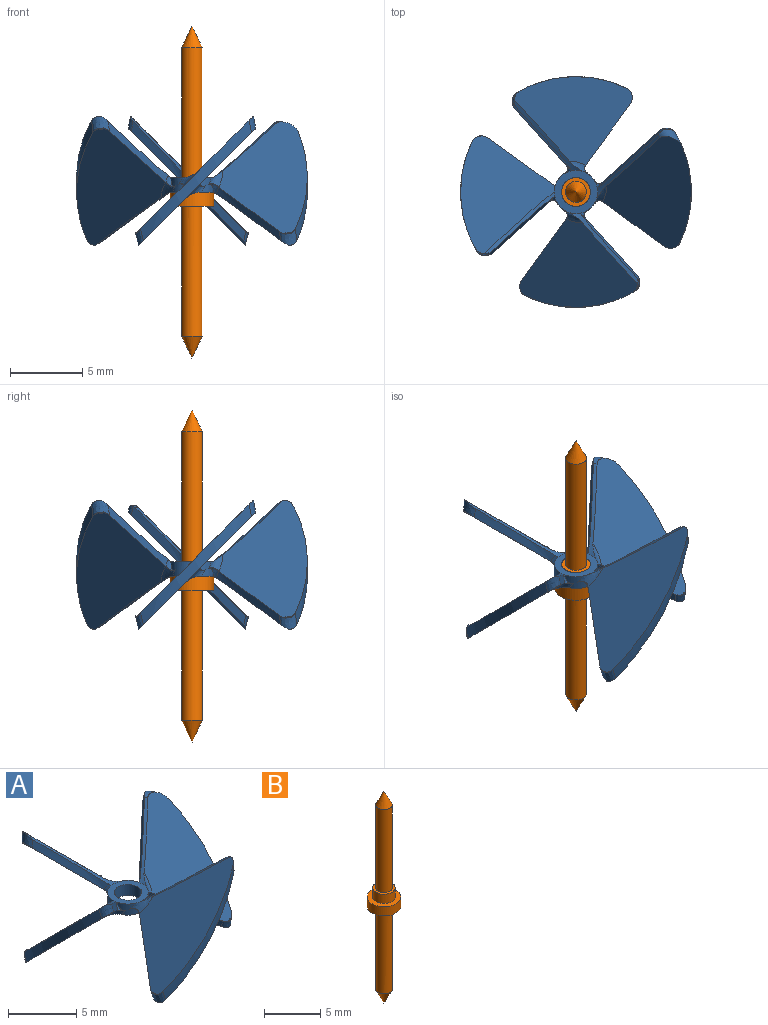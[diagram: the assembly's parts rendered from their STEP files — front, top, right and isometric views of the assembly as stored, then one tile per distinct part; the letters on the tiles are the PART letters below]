
ASSEMBLY  parts=2 mates=1
PART A: 58 faces, bbox 16.4x16.4x10.8 mm
  f0: plane 8.57x8.57mm, normal (-0.71,0,0.71), area 43.5mm2, adj f17,f24,f31,f43,f54,f55
  f1: plane 8.54x8.54mm, normal (0.71,0,-0.71), area 42.7mm2, adj f9,f24,f32,f35,f54,f55
  f2: plane 8.54x8.54mm, normal (-0.71,0,-0.71), area 43.2mm2, adj f8,f25,f29,f37,f52,f53
  f3: plane 8.57x8.57mm, normal (0.71,0,0.71), area 41mm2, adj f16,f25,f30,f45,f52,f53
  f4: plane 8.22x8.22mm, normal (0,0.71,-0.71), area 43.2mm2, adj f10,f23,f27,f39,f50,f51
  f5: plane 8.17x8.17mm, normal (0,-0.71,0.71), area 40.6mm2, adj f18,f23,f28,f41,f49,f51
  f6: plane 8.74x8.74mm, normal (0,0.71,0.71), area 43.7mm2, adj f15,f20,f22,f47,f56,f57
  f7: plane 8.54x8.54mm, normal (0,-0.71,-0.71), area 42.7mm2, adj f11,f22,f26,f33,f56,f57
  f8: cone r=9mm half-angle=59deg, axis (0,0,-1), area 1.9mm2, adj f2,f21,f29,f45,f46,f53
  f9: cone r=9mm half-angle=59deg, axis (0,0,-1), area 1.9mm2, adj f1,f21,f32,f43,f44,f55
  f10: cone r=9mm half-angle=59deg, axis (0,0,-1), area 1.9mm2, adj f4,f21,f27,f41,f42,f51
  f11: cone r=9mm half-angle=59deg, axis (0,0,-1), area 2.1mm2, adj f7,f21,f26,f47,f57
  f12: cylinder r=1.5mm len=1.14mm, axis (0,0,-1), area 0.9mm2, adj f19,f21,f26,f31,f34,f44
  f13: cylinder r=1.5mm len=1.14mm, axis (0,0,-1), area 0.9mm2, adj f19,f21,f28,f32,f36,f42
  f14: cylinder r=1.5mm len=1.14mm, axis (0,0,-1), area 0.9mm2, adj f19,f21,f27,f30,f40,f46
  f15: cylinder r=1.5mm len=1.46mm, axis (0,0,-1), area 1.3mm2, adj f6,f19,f21,f29,f38,f47
  f16: cone r=8mm half-angle=55.3deg, axis (0,0,1), area 2mm2, adj f3,f19,f30,f37,f38,f52
  f17: cone r=8mm half-angle=55.3deg, axis (0,0,1), area 2mm2, adj f0,f19,f31,f35,f36,f54
  f18: cone r=8mm half-angle=55.3deg, axis (0,0,1), area 1.9mm2, adj f5,f19,f28,f39,f40,f49
  f19: plane 3x3mm, normal (0,0,1), area 3.9mm2, adj f12,f13,f14,f15,f16,f17,f18,f20
  f20: cone r=8mm half-angle=55.3deg, axis (0,0,1), area 1.9mm2, adj f6,f19,f33,f34,f56
  f21: plane 3x3mm, normal (0,0,-1), area 3.9mm2, adj f8,f9,f10,f11,f12,f13,f14,f15
  f22: cylinder r=8mm len=8.31mm, axis (0,0,1), area 7.9mm2, adj f6,f7,f56,f57
  f23: cylinder r=8mm len=7.68mm, axis (0,0,1), area 7.4mm2, adj f4,f5,f49,f50,f51
  f24: cylinder r=8mm len=8.32mm, axis (0,0,1), area 7.9mm2, adj f0,f1,f54,f55
  f25: cylinder r=8mm len=8.32mm, axis (0,0,1), area 7.9mm2, adj f2,f3,f52,f53
  f26: bspline ~1.75x1.35mm, area 0.7mm2, adj f7,f11,f12,f34
  f27: bspline ~1.75x1.35mm, area 0.7mm2, adj f4,f10,f14,f40
  f28: bspline ~1.87x1.45mm, area 0.8mm2, adj f5,f13,f18,f42
  f29: bspline ~1.75x1.35mm, area 0.7mm2, adj f2,f8,f15,f38
  f30: bspline ~1.87x1.45mm, area 0.8mm2, adj f3,f14,f16,f46
  f31: bspline ~1.87x1.45mm, area 0.8mm2, adj f0,f12,f17,f44
  f32: bspline ~1.75x1.35mm, area 0.7mm2, adj f1,f9,f13,f36
  f33: bspline ~4.28x4.19mm, area 3.7mm2, adj f7,f20,f34,f56
  f34: bspline ~1.02x0.76mm, area 0.2mm2, adj f12,f20,f26,f33
  f35: bspline ~4.28x4.19mm, area 3.7mm2, adj f1,f17,f36,f54
  f36: bspline ~1.02x0.76mm, area 0.2mm2, adj f13,f17,f32,f35
  f37: bspline ~4.28x4.19mm, area 3.7mm2, adj f2,f16,f38,f52
  f38: bspline ~1.02x0.76mm, area 0.2mm2, adj f15,f16,f29,f37
  f39: bspline ~5.22x5.08mm, area 3.7mm2, adj f4,f18,f40,f49,f50
  f40: bspline ~1.02x0.76mm, area 0.2mm2, adj f14,f18,f27,f39
  f41: bspline ~5.59x4.45mm, area 3.6mm2, adj f5,f10,f42,f51
  f42: bspline ~1.04x0.71mm, area 0.2mm2, adj f10,f13,f28,f41
  f43: bspline ~5.59x4.45mm, area 3.6mm2, adj f0,f9,f44,f55
  f44: bspline ~1.04x0.71mm, area 0.2mm2, adj f9,f12,f31,f43
  f45: bspline ~5.59x4.45mm, area 3.6mm2, adj f3,f8,f46,f53
  f46: bspline ~1.04x0.71mm, area 0.2mm2, adj f8,f14,f30,f45
  f47: bspline ~4.98x3.96mm, area 3.8mm2, adj f6,f11,f15,f57
  f48: cylinder r=1mm len=2mm, axis (0,0,1), area 6.3mm2, adj f19,f21
  f49: torus R=7.3mm, axis (0,0,1), area 1mm2, adj f5,f18,f23,f39,f50
  f50: bspline ~1.24x1.19mm, area 0.4mm2, adj f4,f23,f39,f49
  f51: bspline ~2.1x1.32mm, area 1.2mm2, adj f4,f5,f10,f23,f41
  f52: bspline ~2.11x1.34mm, area 1.3mm2, adj f2,f3,f16,f25,f37
  f53: bspline ~2.1x1.32mm, area 1.2mm2, adj f2,f3,f8,f25,f45
  f54: bspline ~2.11x1.34mm, area 1.3mm2, adj f0,f1,f17,f24,f35
  f55: bspline ~2.1x1.32mm, area 1.2mm2, adj f0,f1,f9,f24,f43
  f56: bspline ~2.11x1.34mm, area 1.3mm2, adj f6,f7,f20,f22,f33
  f57: bspline ~1.91x1.3mm, area 1.2mm2, adj f6,f7,f11,f22,f47
PART B: 9 faces, bbox 3x3x23 mm
  f0: cone r=0.73mm half-angle=25.8deg, axis (0,0,-1), area 3.8mm2, adj f1
  f1: cylinder r=0.73mm len=9mm, axis (0,0,-1), area 41mm2, adj f0,f2
  f2: plane 2x2mm, normal (0,0,1), area 1.5mm2, adj f1,f3
  f3: cylinder r=1mm len=2mm, axis (0,0,-1), area 6.3mm2, adj f2,f4
  f4: plane 3x3mm, normal (0,0,1), area 3.9mm2, adj f3,f5
  f5: cylinder r=1.5mm len=3mm, axis (0,0,-1), area 9.4mm2, adj f4,f6
  f6: plane 3x3mm, normal (0,0,-1), area 5.4mm2, adj f5,f7
  f7: cylinder r=0.73mm len=9mm, axis (0,0,-1), area 41mm2, adj f6,f8
  f8: cone r=0.73mm half-angle=25.8deg, axis (0,0,1), area 3.8mm2, adj f7
PLACE A t=(-4.46,-1.04,2.3)mm
PLACE B t=(-4.46,-1.04,0.8)mm
MATE fastened B.f8 <-> A.f48  axis (0,0,1) through (-4.46,-1.04,1.8)mm
